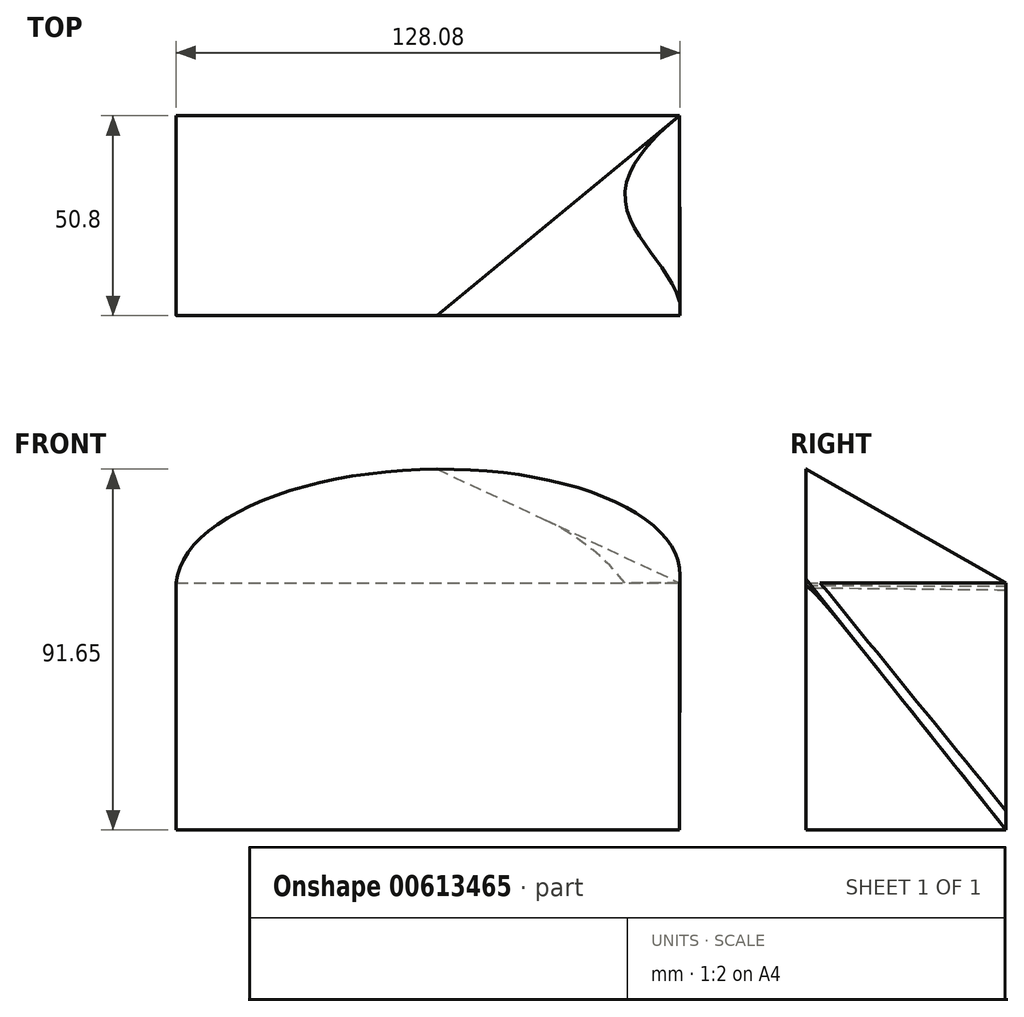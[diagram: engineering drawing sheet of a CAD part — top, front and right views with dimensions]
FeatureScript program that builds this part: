
annotation { "Feature Type Name" : "Feature", "Feature Type Description" : "" }
export const myFeature = defineFeature(function(context is Context, id is Id, definition is map)
    precondition{}
    {
        {
            var Q0;
            Q0=qCreatedBy(makeId("Front.planeOp"),FACE);
            var sketch = newSketch(context, id + "F0", { "sketchPlane" : qUnion([Q0])});
            skLineSegment(sketch, "E0.bottom", {"start": v(-64.03, 27.62) * mm, "end": v(63.8, 27.62) * mm});
            skLineSegment(sketch, "E0.top", {"start": v(-64.03, -35.15) * mm, "end": v(63.8, -35.15) * mm});
            skLineSegment(sketch, "E0.left", {"start": v(-64.03, 27.62) * mm, "end": v(-64.03, -35.15) * mm});
            skLineSegment(sketch, "E0.right", {"start": v(63.8, 27.62) * mm, "end": v(63.8, -35.15) * mm});
            skSolve(sketch);
        }
        {
            var Q0;
            Q0=makeQuery(id+"F0.imprint","IMPRINT",FACE,{"disambiguationData":[TD([[makeQuery(id+"F0.imprint","IMPRINT",EDGE,{"derivedFrom":sQuery(id+"F0.wireOp",EDGE,"E0.bottom")}),-1.0]])]});
            extrude(context, id + "F1", {"entities" : qUnion([Q0]), "oppositeDirection" : true, "depth" : 50.8 * mm, "offsetDistance" : 25.4 * mm});
        }
        {
            var Q0;
            Q0=qCreatedBy(makeId("Front.planeOp"),FACE);
            var sketch = newSketch(context, id + "F2", { "sketchPlane" : qUnion([Q0])});
            skEllipse(sketch, "E1", {"center": v(0, 28.08) * mm, "majorRadius": 64.06 * mm, "minorRadius": 28.38 * mm, "majorAxis": v(1, 0.03)});
            skSolve(sketch);
        }
        {
            var Q0;
            Q0=makeQuery(id+"F2.imprint","IMPRINT",FACE,{"disambiguationData":[TD([[makeQuery(id+"F2.imprint","IMPRINT",EDGE,{"derivedFrom":sQuery(id+"F2.wireOp",EDGE,"E1")}),1.0]])]});
            var Q1;
            Q1=makeQuery(id+"F1.opExtrude","CAP_FACE",FACE,{"disambiguationData":[OSD([sQuery(id+"F0.wireOp",EDGE,"E0.bottom"),sQuery(id+"F0.wireOp",EDGE,"E0.top"),sQuery(id+"F0.wireOp",EDGE,"E0.left"),sQuery(id+"F0.wireOp",EDGE,"E0.right")])],"isStart":false});
            loft(context, id + "F3", {"operationType" : NewBodyOperationType.ADD, "sheetProfilesArray" : [{ "sheetProfileEntities" : qUnion([Q0]) }, { "sheetProfileEntities" : qUnion([Q1]) }]});
        }
    });
